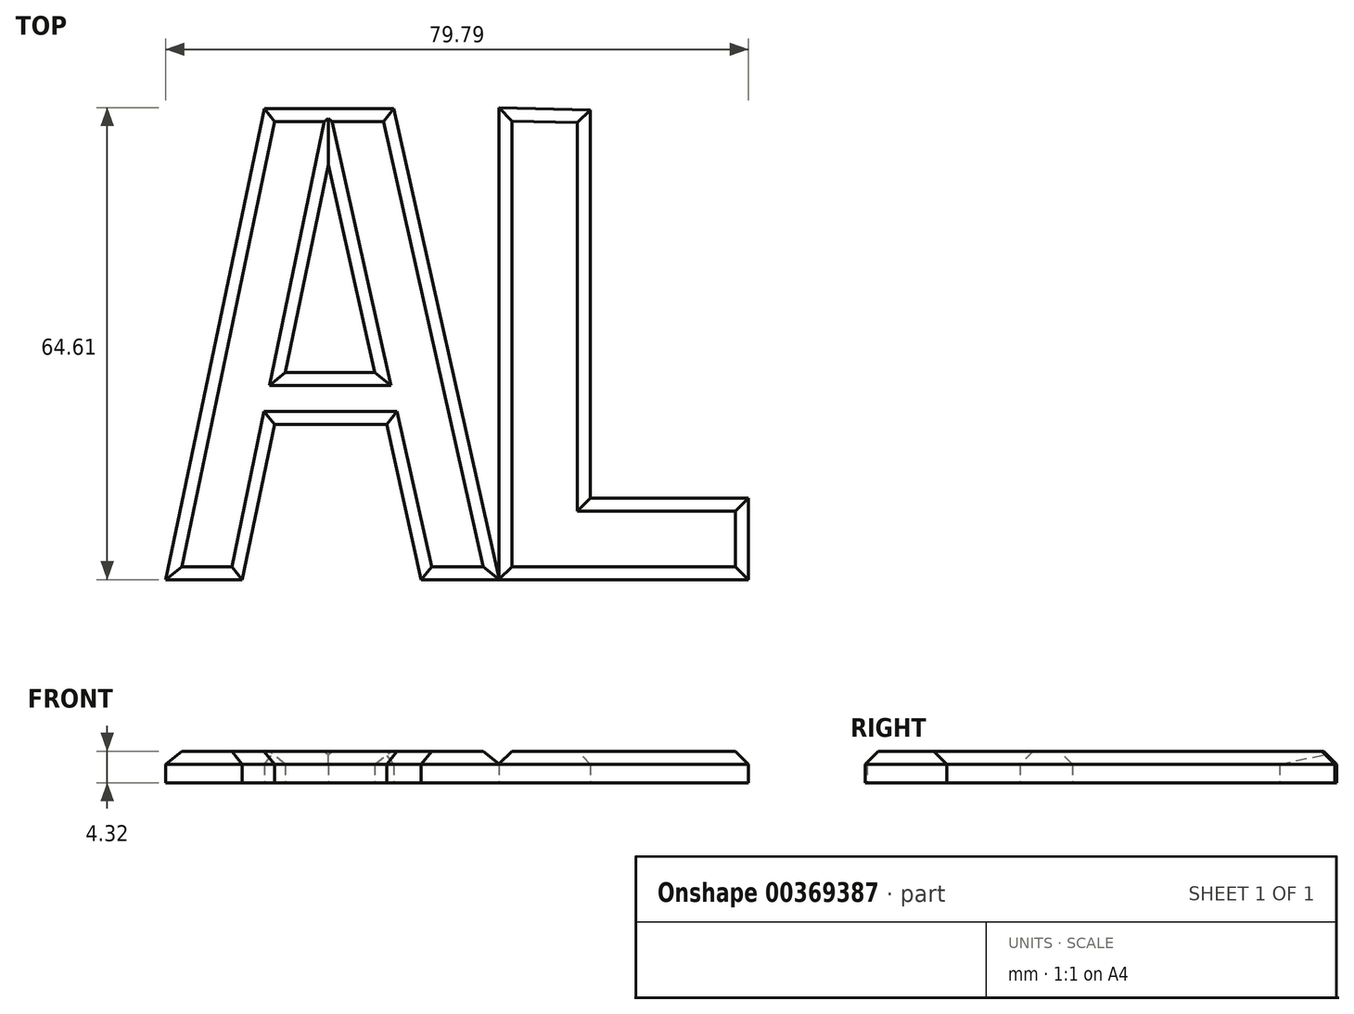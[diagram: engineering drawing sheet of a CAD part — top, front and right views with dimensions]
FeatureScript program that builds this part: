
annotation { "Feature Type Name" : "Feature", "Feature Type Description" : "" }
export const myFeature = defineFeature(function(context is Context, id is Id, definition is map)
    precondition{}
    {
        {
            var Q0;
            Q0=qCreatedBy(makeId("Top.planeOp"),FACE);
            var sketch = newSketch(context, id + "F0", { "sketchPlane" : qUnion([Q0])});
            skLineSegment(sketch, "E0", {"start": v(-56.61, 0) * mm, "end": v(-44.8, 56.78) * mm});
            skLineSegment(sketch, "E1", {"start": v(-44.8, 56.78) * mm, "end": v(-32.1, 0) * mm});
            skLineSegment(sketch, "E2", {"start": v(-32.1, 0) * mm, "end": v(-21.42, 0) * mm});
            skLineSegment(sketch, "E3", {"start": v(-21.42, 0) * mm, "end": v(-34.12, 56.78) * mm});
            skLineSegment(sketch, "E4", {"start": v(-34.12, 56.78) * mm, "end": v(-35.85, 64.5) * mm});
            skLineSegment(sketch, "E5", {"start": v(-35.85, 64.5) * mm, "end": v(-53.6, 64.5) * mm});
            skLineSegment(sketch, "E6", {"start": v(-53.6, 64.5) * mm, "end": v(-67.1, 0) * mm});
            skLineSegment(sketch, "E7", {"start": v(-67.1, 0) * mm, "end": v(-56.61, 0) * mm});
            skLineSegment(sketch, "E8", {"start": v(-50.7, 28.39) * mm, "end": v(-38.45, 28.39) * mm});
            skLineSegment(sketch, "E9", {"start": v(-38.45, 28.39) * mm, "end": v(-36.85, 21.25) * mm});
            skLineSegment(sketch, "E10", {"start": v(-36.85, 21.25) * mm, "end": v(-52.2, 21.25) * mm});
            skLineSegment(sketch, "E11", {"start": v(-21.48, 64.61) * mm, "end": v(-21.48, 0) * mm});
            skLineSegment(sketch, "E12", {"start": v(-21.48, 0) * mm, "end": v(12.7, 0) * mm});
            skLineSegment(sketch, "E13", {"start": v(12.7, 0) * mm, "end": v(12.7, 11.17) * mm});
            skLineSegment(sketch, "E14", {"start": v(12.7, 11.17) * mm, "end": v(-8.92, 11.17) * mm});
            skLineSegment(sketch, "E15", {"start": v(-8.92, 11.17) * mm, "end": v(-8.92, 64.32) * mm});
            skLineSegment(sketch, "E16", {"start": v(-8.92, 64.32) * mm, "end": v(-21.48, 64.61) * mm});
            skSolve(sketch);
        }
        {
            var Q0;
            Q0 = qSketchRegion(id + "F0", true);
            extrude(context, id + "F1", {"entities" : qUnion([Q0]), "depth" : 4.32 * mm});
        }
        {
            var Q0;
            Q0=makeQuery(id+"F1.opExtrude","CAP_EDGE",EDGE,{"disambiguationData":[OSD([sQuery(id+"F0.wireOp",EDGE,"E6")])],"isStart":false});
            var Q1;
            Q1=makeQuery(id+"F1.opExtrude","CAP_EDGE",EDGE,{"disambiguationData":[OSD([sQuery(id+"F0.wireOp",EDGE,"E3"),sQuery(id+"F0.wireOp",EDGE,"E4")])],"isStart":false});
            var Q2;
            Q2=makeQuery(id+"F1.opExtrude","CAP_EDGE",EDGE,{"disambiguationData":[OSD([sQuery(id+"F0.wireOp",EDGE,"E5")])],"isStart":false});
            var Q3;
            {var subQ0=sQuery(id+"F0.wireOp",EDGE,"E0");Q3=makeQuery(id+"F1.opExtrude","CAP_EDGE",EDGE,{"disambiguationData":[OSD([subQ0]),TDD([makeQuery(id+"F0.imprint","IMPRINT",EDGE,{"disambiguationData":[TD([[makeQuery(id+"F0.imprint","INTERSECT",VERTEX,{"derivedFrom":[subQ0,sQuery(id+"F0.wireOp",EDGE,"E7")]}),-1.0]])],"derivedFrom":subQ0})])],"isStart":false});}
            var Q4;
            Q4=makeQuery(id+"F1.opExtrude","CAP_EDGE",EDGE,{"disambiguationData":[OSD([sQuery(id+"F0.wireOp",EDGE,"E10")])],"isStart":false});
            var Q5;
            {var subQ0=sQuery(id+"F0.wireOp",EDGE,"E1");Q5=makeQuery(id+"F1.opExtrude","CAP_EDGE",EDGE,{"disambiguationData":[OSD([subQ0]),TDD([makeQuery(id+"F0.imprint","IMPRINT",EDGE,{"disambiguationData":[TD([[makeQuery(id+"F0.imprint","INTERSECT",VERTEX,{"derivedFrom":[subQ0,sQuery(id+"F0.wireOp",EDGE,"E2")]}),1.0]])],"derivedFrom":subQ0})])],"isStart":false});}
            var Q6;
            Q6=makeQuery(id+"F1.opExtrude","CAP_FACE",FACE,{"disambiguationData":[OSD([sQuery(id+"F0.wireOp",EDGE,"E0"),sQuery(id+"F0.wireOp",EDGE,"E1"),sQuery(id+"F0.wireOp",EDGE,"E2"),sQuery(id+"F0.wireOp",EDGE,"E3"),sQuery(id+"F0.wireOp",EDGE,"E4"),sQuery(id+"F0.wireOp",EDGE,"E5"),sQuery(id+"F0.wireOp",EDGE,"E6"),sQuery(id+"F0.wireOp",EDGE,"E7"),sQuery(id+"F0.wireOp",EDGE,"E8"),sQuery(id+"F0.wireOp",EDGE,"E10"),sQuery(id+"F0.wireOp",EDGE,"E11"),sQuery(id+"F0.wireOp",EDGE,"E12"),sQuery(id+"F0.wireOp",EDGE,"E13"),sQuery(id+"F0.wireOp",EDGE,"E14"),sQuery(id+"F0.wireOp",EDGE,"E15"),sQuery(id+"F0.wireOp",EDGE,"E16")])],"isStart":false});
            chamfer(context, id + "F2", {"entities" : qUnion([Q0, Q1, Q2, Q3, Q4, Q5, Q6]), "width" : 1.78 * mm, "tangentPropagation" : true});
        }
    });
